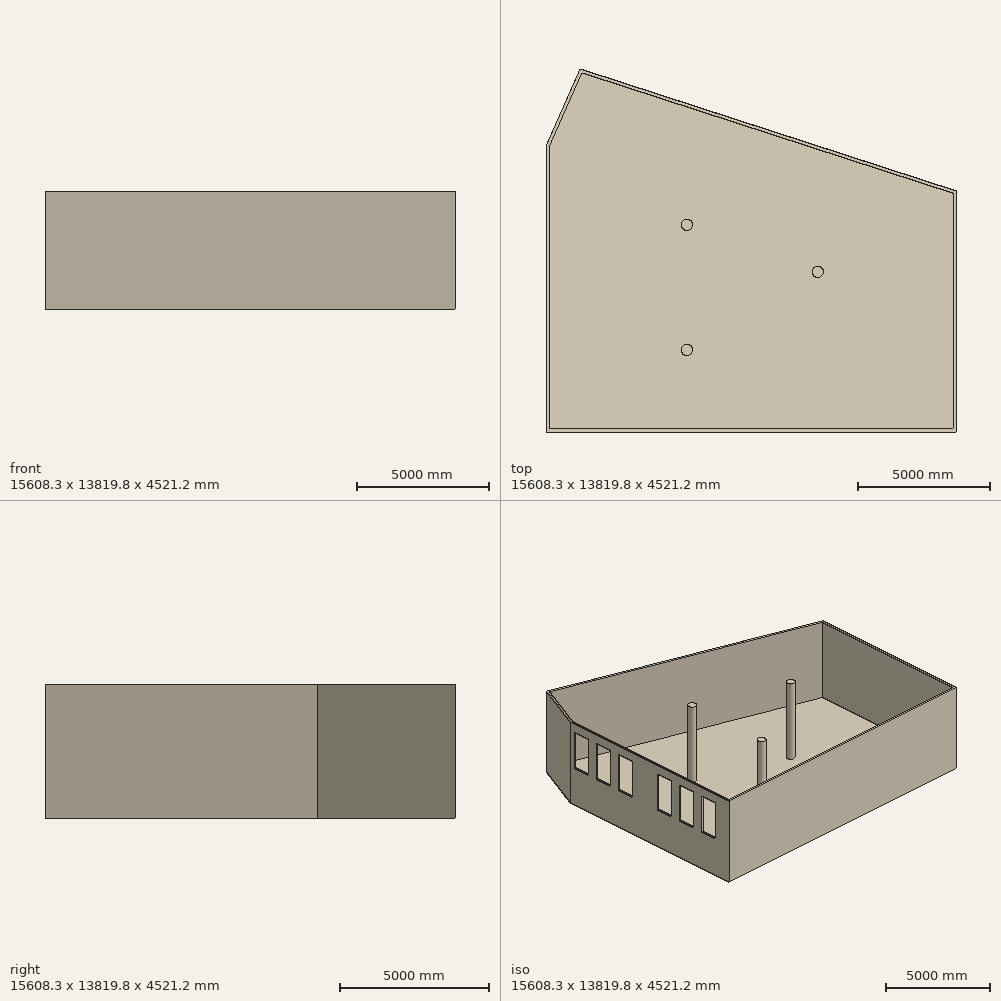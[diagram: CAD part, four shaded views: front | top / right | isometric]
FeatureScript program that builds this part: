
annotation { "Feature Type Name" : "Feature", "Feature Type Description" : "" }
export const myFeature = defineFeature(function(context is Context, id is Id, definition is map)
    precondition{}
    {
        {
            var Q0;
            Q0=qCreatedBy(makeId("Top.planeOp"),FACE);
            var sketch = newSketch(context, id + "F0", { "sketchPlane" : qUnion([Q0])});
            skLineSegment(sketch, "E0", {"start": v(-5232.4, 3003.7) * mm, "end": v(-5232.4, -7759.55) * mm});
            skLineSegment(sketch, "E1", {"start": v(-5232.4, -7759.55) * mm, "end": v(10134.6, -7759.55) * mm});
            skLineSegment(sketch, "E2", {"start": v(10134.6, -7759.55) * mm, "end": v(10134.6, 1206.65) * mm});
            skLineSegment(sketch, "E3", {"start": v(10134.6, 1206.65) * mm, "end": v(-3999.46, 5791.2) * mm});
            skLineSegment(sketch, "E4", {"start": v(-3999.46, 5791.2) * mm, "end": v(-5232.4, 3003.7) * mm});
            skLineSegment(sketch, "E5", {"start": v(0, 0) * mm, "end": v(-5232.4, 0) * mm, "construction": true});
            skLineSegment(sketch, "E6", {"start": v(-3999.46, 5791.2) * mm, "end": v(-3999.46, 0) * mm, "construction": true});
            skLineSegment(sketch, "E7.0", {"start": v(-5353.05, 3029.19) * mm, "end": v(-5353.05, -7880.2) * mm});
            skLineSegment(sketch, "E7.1", {"start": v(-4065.77, 5939.55) * mm, "end": v(-5353.05, 3029.19) * mm});
            skLineSegment(sketch, "E7.2", {"start": v(-5353.05, -7880.2) * mm, "end": v(10255.25, -7880.2) * mm});
            skLineSegment(sketch, "E7.3", {"start": v(10255.25, -7880.2) * mm, "end": v(10255.25, 1294.35) * mm});
            skLineSegment(sketch, "E7.4", {"start": v(10255.25, 1294.35) * mm, "end": v(-4065.77, 5939.55) * mm});
            skSolve(sketch);
        }
        {
            var Q0;
            Q0 = qSketchRegion(id + "F0", true);
            extrude(context, id + "F1", {"entities" : qUnion([Q0]), "depth" : 4216.4 * mm, "offsetDistance" : 25.4 * mm});
        }
        {
            var Q0;
            Q0=makeQuery(id+"F1.opExtrude","CAP_FACE",FACE,{"disambiguationData":[OSD([sQuery(id+"F0.wireOp",EDGE,"E0"),sQuery(id+"F0.wireOp",EDGE,"E1"),sQuery(id+"F0.wireOp",EDGE,"E2"),sQuery(id+"F0.wireOp",EDGE,"E3"),sQuery(id+"F0.wireOp",EDGE,"E4"),sQuery(id+"F0.wireOp",EDGE,"E7.0"),sQuery(id+"F0.wireOp",EDGE,"E7.1"),sQuery(id+"F0.wireOp",EDGE,"E7.2"),sQuery(id+"F0.wireOp",EDGE,"E7.3"),sQuery(id+"F0.wireOp",EDGE,"E7.4")])],"isStart":true});
            var sketch = newSketch(context, id + "F2", { "sketchPlane" : qUnion([Q0])});
            skLineSegment(sketch, "E8", {"start": v(10255.25, -1294.35) * mm, "end": v(10255.25, 7880.2) * mm});
            skLineSegment(sketch, "E9", {"start": v(10255.25, 7880.2) * mm, "end": v(-5353.05, 7880.2) * mm});
            skLineSegment(sketch, "E10", {"start": v(-5353.05, 7880.2) * mm, "end": v(-5353.05, -3029.19) * mm});
            skLineSegment(sketch, "E11", {"start": v(-5353.05, -3029.19) * mm, "end": v(-4065.77, -5939.55) * mm});
            skLineSegment(sketch, "E12", {"start": v(-4065.77, -5939.55) * mm, "end": v(10255.25, -1294.35) * mm});
            skSolve(sketch);
        }
        {
            var Q0;
            Q0=makeQuery(id+"F2.imprint","IMPRINT",FACE,{"disambiguationData":[TD([[makeQuery(id+"F2.imprint","IMPRINT",EDGE,{"derivedFrom":sQuery(id+"F2.wireOp",EDGE,"E8")}),-1.0]])]});
            var Q1;
            Q1=makeQuery(id+"F2.imprint","IMPRINT",FACE,{"disambiguationData":[TD([[makeQuery(id+"F2.imprint","IMPRINT",EDGE,{"derivedFrom":makeQuery(id+"F1.opExtrude","CAP_EDGE",EDGE,{"disambiguationData":[OSD([sQuery(id+"F0.wireOp",EDGE,"E0")])],"isStart":true})}),-1.0]])]});
            extrude(context, id + "F3", {"entities" : qUnion([Q0, Q1]), "operationType" : NewBodyOperationType.ADD, "depth" : 304.8 * mm, "offsetDistance" : 25.4 * mm});
        }
        {
            var Q0;
            Q0=makeQuery(id+"F3.opExtrude","CAP_FACE",FACE,{"disambiguationData":[OSD([sQuery(id+"F2.wireOp",EDGE,"E8"),sQuery(id+"F2.wireOp",EDGE,"E9"),sQuery(id+"F2.wireOp",EDGE,"E10"),sQuery(id+"F2.wireOp",EDGE,"E11"),sQuery(id+"F2.wireOp",EDGE,"E12")])],"isStart":true});
            var sketch = newSketch(context, id + "F4", { "sketchPlane" : qUnion([Q0])});
            skCircle(sketch, "E13", {"center": v(0, 0) * mm, "radius": 215.9 * mm});
            skLineSegment(sketch, "E14", {"start": v(0, 0) * mm, "end": v(-5232.4, 0) * mm, "construction": true});
            skLineSegment(sketch, "E15", {"start": v(-3999.46, 5791.2) * mm, "end": v(-3999.46, 0) * mm, "construction": true});
            skCircle(sketch, "E16", {"center": v(0, -4762.35) * mm, "radius": 215.9 * mm});
            skCircle(sketch, "E17", {"center": v(4978.4, -1790.55) * mm, "radius": 215.9 * mm});
            skLineSegment(sketch, "E18", {"start": v(0, 0) * mm, "end": v(0, -4762.35) * mm, "construction": true});
            skLineSegment(sketch, "E19", {"start": v(4978.4, -1790.55) * mm, "end": v(10134.6, -1790.55) * mm, "construction": true});
            skLineSegment(sketch, "E20", {"start": v(4978.4, -1790.55) * mm, "end": v(4978.4, -7759.55) * mm, "construction": true});
            skLineSegment(sketch, "E21", {"start": v(0, -4762.35) * mm, "end": v(0, -7759.55) * mm, "construction": true});
            skSolve(sketch);
        }
        {
            var Q0;
            Q0 = qSketchRegion(id + "F4", true);
            var Q1;
            Q1=makeQuery(id+"F1.opExtrude","CAP_FACE",FACE,{"disambiguationData":[OSD([sQuery(id+"F0.wireOp",EDGE,"E0"),sQuery(id+"F0.wireOp",EDGE,"E1"),sQuery(id+"F0.wireOp",EDGE,"E2"),sQuery(id+"F0.wireOp",EDGE,"E3"),sQuery(id+"F0.wireOp",EDGE,"E4"),sQuery(id+"F0.wireOp",EDGE,"E7.0"),sQuery(id+"F0.wireOp",EDGE,"E7.1"),sQuery(id+"F0.wireOp",EDGE,"E7.2"),sQuery(id+"F0.wireOp",EDGE,"E7.3"),sQuery(id+"F0.wireOp",EDGE,"E7.4")])],"isStart":false});
            extrude(context, id + "F5", {"entities" : qUnion([Q0]), "operationType" : NewBodyOperationType.ADD, "endBound" : BoundingType.UP_TO_SURFACE, "depth" : 25.4 * mm, "endBoundEntityFace" : qUnion([Q1]), "offsetDistance" : 25.4 * mm});
        }
        {
            var Q0;
            Q0=makeQuery(id+"F1.opExtrude","SWEPT_FACE",FACE,{"disambiguationData":[OSD([sQuery(id+"F0.wireOp",EDGE,"E0")])]});
            var sketch = newSketch(context, id + "F6", { "sketchPlane" : qUnion([Q0])});
            skLineSegment(sketch, "E22.bottom", {"start": v(-6921.35, 3759.2) * mm, "end": v(-5968.85, 3759.2) * mm});
            skLineSegment(sketch, "E22.top", {"start": v(-6921.35, 1727.2) * mm, "end": v(-5968.85, 1727.2) * mm});
            skLineSegment(sketch, "E22.left", {"start": v(-6921.35, 3759.2) * mm, "end": v(-6921.35, 1727.2) * mm});
            skLineSegment(sketch, "E22.right", {"start": v(-5968.85, 3759.2) * mm, "end": v(-5968.85, 1727.2) * mm});
            skSolve(sketch);
        }
        {
            var Q0;
            Q0 = qSketchRegion(id + "F6", true);
            extrude(context, id + "F7", {"entities" : qUnion([Q0]), "operationType" : NewBodyOperationType.REMOVE, "endBound" : BoundingType.THROUGH_ALL, "oppositeDirection" : true, "depth" : 25.4 * mm, "offsetDistance" : 25.4 * mm});
        }
        {
            var Q0;
            Q0=makeQuery(id+"F1.opExtrude","SWEPT_FACE",FACE,{"disambiguationData":[OSD([sQuery(id+"F0.wireOp",EDGE,"E0")])]});
            var sketch = newSketch(context, id + "F8", { "sketchPlane" : qUnion([Q0])});
            skLineSegment(sketch, "E23.bottom", {"start": v(-5410.05, 3759.2) * mm, "end": v(-4457.55, 3759.2) * mm});
            skLineSegment(sketch, "E23.top", {"start": v(-5410.05, 1727.2) * mm, "end": v(-4457.55, 1727.2) * mm});
            skLineSegment(sketch, "E23.left", {"start": v(-5410.05, 3759.2) * mm, "end": v(-5410.05, 1727.2) * mm});
            skLineSegment(sketch, "E23.right", {"start": v(-4457.55, 3759.2) * mm, "end": v(-4457.55, 1727.2) * mm});
            skLineSegment(sketch, "E24.bottom", {"start": v(-3898.75, 3759.2) * mm, "end": v(-2946.25, 3759.2) * mm});
            skLineSegment(sketch, "E24.top", {"start": v(-3898.75, 1727.2) * mm, "end": v(-2946.25, 1727.2) * mm});
            skLineSegment(sketch, "E24.left", {"start": v(-3898.75, 3759.2) * mm, "end": v(-3898.75, 1727.2) * mm});
            skLineSegment(sketch, "E24.right", {"start": v(-2946.25, 3759.2) * mm, "end": v(-2946.25, 1727.2) * mm});
            skLineSegment(sketch, "E25.bottom", {"start": v(-1219.05, 3759.2) * mm, "end": v(-266.55, 3759.2) * mm});
            skLineSegment(sketch, "E25.top", {"start": v(-1219.05, 1727.2) * mm, "end": v(-266.55, 1727.2) * mm});
            skLineSegment(sketch, "E25.left", {"start": v(-1219.05, 3759.2) * mm, "end": v(-1219.05, 1727.2) * mm});
            skLineSegment(sketch, "E25.right", {"start": v(-266.55, 3759.2) * mm, "end": v(-266.55, 1727.2) * mm});
            skLineSegment(sketch, "E26.bottom", {"start": v(292.25, 3759.2) * mm, "end": v(1244.75, 3759.2) * mm});
            skLineSegment(sketch, "E26.top", {"start": v(292.25, 1727.2) * mm, "end": v(1244.75, 1727.2) * mm});
            skLineSegment(sketch, "E26.left", {"start": v(292.25, 3759.2) * mm, "end": v(292.25, 1727.2) * mm});
            skLineSegment(sketch, "E26.right", {"start": v(1244.75, 3759.2) * mm, "end": v(1244.75, 1727.2) * mm});
            skLineSegment(sketch, "E27.bottom", {"start": v(1803.55, 3759.2) * mm, "end": v(2756.05, 3759.2) * mm});
            skLineSegment(sketch, "E27.top", {"start": v(1803.55, 1727.2) * mm, "end": v(2756.05, 1727.2) * mm});
            skLineSegment(sketch, "E27.left", {"start": v(1803.55, 3759.2) * mm, "end": v(1803.55, 1727.2) * mm});
            skLineSegment(sketch, "E27.right", {"start": v(2756.05, 3759.2) * mm, "end": v(2756.05, 1727.2) * mm});
            skLineSegment(sketch, "E28", {"start": v(-5968.85, 3759.2) * mm, "end": v(-5410.05, 3759.2) * mm});
            skLineSegment(sketch, "E29", {"start": v(-4457.55, 3759.2) * mm, "end": v(-3898.75, 3759.2) * mm});
            skLineSegment(sketch, "E30", {"start": v(-2946.25, 3759.2) * mm, "end": v(-1219.05, 3759.2) * mm});
            skLineSegment(sketch, "E31", {"start": v(-266.55, 3759.2) * mm, "end": v(292.25, 3759.2) * mm});
            skLineSegment(sketch, "E32", {"start": v(1244.75, 3759.2) * mm, "end": v(1803.55, 3759.2) * mm});
            skSolve(sketch);
        }
        {
            var Q0;
            Q0 = qSketchRegion(id + "F8", true);
            extrude(context, id + "F9", {"entities" : qUnion([Q0]), "operationType" : NewBodyOperationType.REMOVE, "endBound" : BoundingType.THROUGH_ALL, "oppositeDirection" : true, "depth" : 25.4 * mm, "offsetDistance" : 25.4 * mm});
        }
    });
